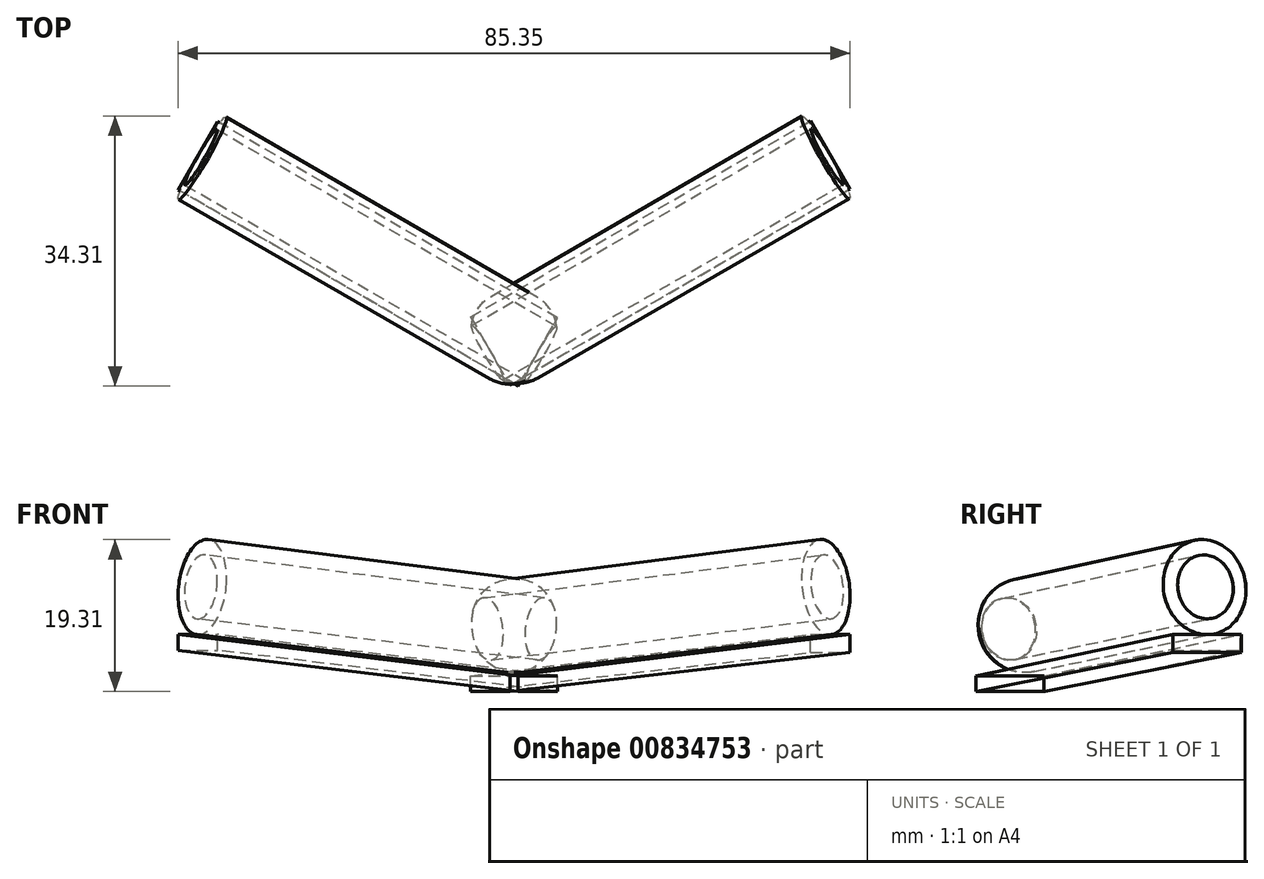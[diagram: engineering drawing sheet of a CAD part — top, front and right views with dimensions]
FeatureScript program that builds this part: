
annotation { "Feature Type Name" : "Feature", "Feature Type Description" : "" }
export const myFeature = defineFeature(function(context is Context, id is Id, definition is map)
    precondition{}
    {
        {
            var Q0;
            Q0=qCreatedBy(makeId("Front.planeOp"),FACE);
            var sketch = newSketch(context, id + "F0", { "sketchPlane" : qUnion([Q0])});
            skLineSegment(sketch, "E0", {"start": v(0, 16.98) * mm, "end": v(0, -4.1) * mm});
            skSolve(sketch);
        }
        {
            var Q0;
            Q0=qCreatedBy(makeId("Right.planeOp"),FACE);
            var Q1;
            Q1=sQuery(id+"F0.wireOp",EDGE,"E0");
            cPlane(context, id + "F1", {"entities" : qUnion([Q0, Q1]), "cplaneType" : CPlaneType.LINE_ANGLE, "offset" : 25 * mm, "angle" : 60 * degree, "width" : 150 * mm, "height" : 150 * mm});
        }
        {
            var Q0;
            Q0=qCreatedBy(id+"F1.planeOp",FACE);
            var sketch = newSketch(context, id + "F2", { "sketchPlane" : qUnion([Q0])});
            skLineSegment(sketch, "E1", {"start": v(3.39, 2) * mm, "end": v(3.39, 4) * mm});
            skLineSegment(sketch, "E2", {"start": v(3.39, 4) * mm, "end": v(3.39, 8) * mm});
            skLineSegment(sketch, "E3", {"start": v(3.39, 0) * mm, "end": v(3.39, 2) * mm});
            skLineSegment(sketch, "E4", {"start": v(0.39, 0) * mm, "end": v(50.25, 0) * mm});
            skLineSegment(sketch, "E5.MirrorCS", {"start": v(3.39, 8) * mm, "end": v(-46.38, 13.33) * mm});
            skLineSegment(sketch, "E6.MirrorCS", {"start": v(-46.48, 10.24) * mm, "end": v(-46.48, 14.24) * mm});
            skLineSegment(sketch, "E7.MirrorCS", {"start": v(3.39, 2) * mm, "end": v(-46.48, 7.24) * mm});
            skLineSegment(sketch, "E8.MirrorCS", {"start": v(3.39, 4) * mm, "end": v(-46.48, 9.24) * mm});
            skLineSegment(sketch, "E9.MirrorCS", {"start": v(-46.48, 3) * mm, "end": v(-46.48, 8.24) * mm});
            skLineSegment(sketch, "E10.MirrorCS", {"start": v(3.39, 0) * mm, "end": v(-46.48, 0) * mm});
            skLineSegment(sketch, "E11.MirrorCS", {"start": v(3.39, 2) * mm, "end": v(-46.48, 2) * mm});
            skLineSegment(sketch, "E12.MirrorCS", {"start": v(-46.48, 0) * mm, "end": v(-46.48, 3) * mm});
            skLineSegment(sketch, "E13.MirrorCS", {"start": v(-46.48, 8.24) * mm, "end": v(-46.48, 10.24) * mm});
            skPoint(sketch, "E14", {"position": v(-17.05, -12.14) * mm});
            skLineSegment(sketch, "E15", {"start": v(3.39, 0) * mm, "end": v(-46.48, 4.95) * mm});
            skSolve(sketch);
        }
        {
            var Q0;
            Q0=makeQuery(id+"F2.imprint","IMPRINT",FACE,{"disambiguationData":[TD([[makeQuery(id+"F2.imprint","IMPRINT",EDGE,{"derivedFrom":sQuery(id+"F2.wireOp",EDGE,"E7.MirrorCS")}),1.0]])]});
            var Q1;
            {var subQ0=sQuery(id+"F2.wireOp",EDGE,"E3");Q1=makeQuery(id+"F2.imprint","IMPRINT",FACE,{"disambiguationData":[TD([[makeQuery(id+"F2.imprint","IMPRINT",EDGE,{"derivedFrom":subQ0}),1.0]])]});}
            extrude(context, id + "F3", {"entities" : qUnion([Q0, Q1]), "endBound" : BoundingType.SYMMETRIC, "depth" : 10 * mm, "offsetDistance" : 25 * mm});
        }
        {
            var Q0;
            {var subQ0=sQuery(id+"F2.wireOp",EDGE,"E8.MirrorCS");Q0=makeQuery(id+"F2.imprint","IMPRINT",FACE,{"disambiguationData":[TD([[makeQuery(id+"F2.imprint","IMPRINT",EDGE,{"derivedFrom":subQ0}),1.0]])]});}
            var Q1;
            {var subQ0=sQuery(id+"F2.wireOp",EDGE,"E7.MirrorCS");Q1=makeQuery(id+"F2.imprint","IMPRINT",FACE,{"disambiguationData":[TD([[makeQuery(id+"F2.imprint","IMPRINT",EDGE,{"derivedFrom":subQ0}),-1.0]])]});}
            var Q2;
            Q2=sQuery(id+"F2.wireOp",EDGE,"E5.MirrorCS");
            revolve(context, id + "F4", {"operationType" : NewBodyOperationType.ADD, "surfaceOperationType" : NewSurfaceOperationType.NEW, "entities" : qUnion([Q0, Q1]), "axis" : qUnion([Q2]), "revolveType" : RevolveType.FULL});
        }
        {
            var Q0;
            Q0=qCreatedBy(makeId("Right.planeOp"),FACE);
            var Q1;
            Q1=sQuery(id+"F0.wireOp",EDGE,"E0");
            cPlane(context, id + "F5", {"entities" : qUnion([Q0, Q1]), "cplaneType" : CPlaneType.LINE_ANGLE, "offset" : 25 * mm, "angle" : 60 * degree, "oppositeDirection" : true, "width" : 150 * mm, "height" : 150 * mm});
        }
        {
            var Q0;
            Q0=qCreatedBy(id+"F5.planeOp",FACE);
            var sketch = newSketch(context, id + "F6", { "sketchPlane" : qUnion([Q0])});
            skLineSegment(sketch, "E16", {"start": v(3.6, 2) * mm, "end": v(3.6, 4) * mm});
            skLineSegment(sketch, "E17", {"start": v(3.6, 4) * mm, "end": v(3.6, 8) * mm});
            skLineSegment(sketch, "E18", {"start": v(3.6, 0) * mm, "end": v(3.6, 2) * mm});
            skLineSegment(sketch, "E19", {"start": v(-0.2, 0) * mm, "end": v(49.67, 0) * mm});
            skLineSegment(sketch, "E20.MirrorCS", {"start": v(3.6, 8) * mm, "end": v(-46.16, 13.33) * mm});
            skLineSegment(sketch, "E21.MirrorCS", {"start": v(-46.25, 10.24) * mm, "end": v(-46.25, 14.24) * mm});
            skLineSegment(sketch, "E22.MirrorCS", {"start": v(3.6, 2) * mm, "end": v(-46.25, 7.24) * mm});
            skLineSegment(sketch, "E23.MirrorCS", {"start": v(3.6, 4) * mm, "end": v(-46.25, 9.24) * mm});
            skLineSegment(sketch, "E24.MirrorCS", {"start": v(-46.25, 3) * mm, "end": v(-46.25, 8.24) * mm});
            skLineSegment(sketch, "E25.MirrorCS", {"start": v(3.6, 0) * mm, "end": v(-46.25, 0) * mm});
            skLineSegment(sketch, "E26.MirrorCS", {"start": v(3.6, 2) * mm, "end": v(-46.25, 2) * mm});
            skLineSegment(sketch, "E27.MirrorCS", {"start": v(-46.25, 0) * mm, "end": v(-46.25, 2) * mm});
            skLineSegment(sketch, "E28.MirrorCS", {"start": v(-46.25, 8.24) * mm, "end": v(-46.25, 10.24) * mm});
            skLineSegment(sketch, "E29", {"start": v(-46.25, 2) * mm, "end": v(-46.25, 3) * mm});
            skLineSegment(sketch, "E30", {"start": v(3.6, 0) * mm, "end": v(-46.25, 5.24) * mm});
            skSolve(sketch);
        }
        {
            var Q0;
            Q0=makeQuery(id+"F6.imprint","IMPRINT",FACE,{"disambiguationData":[TD([[makeQuery(id+"F6.imprint","IMPRINT",EDGE,{"derivedFrom":sQuery(id+"F6.wireOp",EDGE,"E22.MirrorCS")}),1.0]])]});
            var Q1;
            {var subQ0=sQuery(id+"F6.wireOp",EDGE,"E18");Q1=makeQuery(id+"F6.imprint","IMPRINT",FACE,{"disambiguationData":[TD([[makeQuery(id+"F6.imprint","IMPRINT",EDGE,{"derivedFrom":subQ0}),1.0]])]});}
            extrude(context, id + "F7", {"entities" : qUnion([Q0, Q1]), "endBound" : BoundingType.SYMMETRIC, "depth" : 10 * mm, "offsetDistance" : 25 * mm});
        }
        {
            var Q0;
            Q0=makeQuery(id+"F6.imprint","IMPRINT",FACE,{"disambiguationData":[TD([[makeQuery(id+"F6.imprint","IMPRINT",EDGE,{"derivedFrom":sQuery(id+"F6.wireOp",EDGE,"E16")}),1.0]])]});
            var Q1;
            Q1=sQuery(id+"F6.wireOp",EDGE,"E20.MirrorCS");
            revolve(context, id + "F8", {"surfaceOperationType" : NewSurfaceOperationType.NEW, "entities" : qUnion([Q0]), "axis" : qUnion([Q1]), "revolveType" : RevolveType.FULL});
        }
        {
            var Q0;
            Q0=makeQuery(id+"F4.opRevolve","SWEPT_EDGE",EDGE,{"disambiguationData":[OSD([sQuery(id+"F2.wireOp",EDGE,"E1"),sQuery(id+"F2.wireOp",EDGE,"E3"),sQuery(id+"F2.wireOp",EDGE,"E7.MirrorCS"),sQuery(id+"F2.wireOp",EDGE,"E11.MirrorCS")])]});
            var Q1;
            Q1=makeQuery(id+"F8.opRevolve","SWEPT_EDGE",EDGE,{"disambiguationData":[OSD([sQuery(id+"F6.wireOp",EDGE,"E16"),sQuery(id+"F6.wireOp",EDGE,"E18"),sQuery(id+"F6.wireOp",EDGE,"E22.MirrorCS"),sQuery(id+"F6.wireOp",EDGE,"E26.MirrorCS")])]});
            var Q2;
            Q2=makeQuery(id+"FcDGojZFEvCuKsQ_3.opExtrude","CAP_EDGE",EDGE,{"disambiguationData":[OSD([sQuery(id+"F6.wireOp",EDGE,"E18")])],"isStart":false});
            var Q3;
            Q3=makeQuery(id+"F9EvrPw9UCSVND9_1.opExtrude","CAP_EDGE",EDGE,{"disambiguationData":[OSD([sQuery(id+"F2.wireOp",EDGE,"E3")])],"isStart":true});
            fillet(context, id + "F9", {"entities" : qUnion([Q0, Q1, Q2, Q3]), "radius" : 5 * mm, "tangentPropagation" : true, "allowEdgeOverflow" : false});
        }
    });
